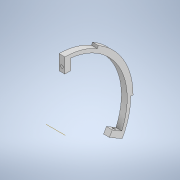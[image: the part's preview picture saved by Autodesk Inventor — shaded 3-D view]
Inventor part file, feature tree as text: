
AUTODESK INVENTOR PART (.ipt)
format: ipt  version: 2021 (Build 250183000, 183)  size: 156,672 bytes
history: native  units: in
note: dims shown in document units (in); Inventor stores cm internally (conversion verified against a paired STEP export)
features: hole x2, other x2, sketch x2, extrude x1
ambient origin geometry x8: Origin, YZ Plane, XZ Plane, XY Plane, X Axis, Y Axis, Z Axis, Center Point
bodies: Body1 (feature_tree)
feature tree (7):
  extrude  "Extrusion2"  TaperAngle=30.0deg  [1 undecoded]
  hole  "Hole1"  [1 undecoded]
  hole  "Hole2"  [1 undecoded]
  other  "Insert Center"
  other  "Part"
  sketch  "Sketch5"  dims[d29=2.375in d32=30.0deg]
  sketch  "Sketch6"  dims[d34=2.175in d35=0.2in d37=60.0deg d38=2.175in d42=0.59in d44=0.4134in d45=2.2963in d46=0.2in d47=0.0in d48=0.3346in d49=0.096in d50=0.75in d51=0.172in d52=0.25in d53=0.5635in d54=0.484in d55=0.8108in d56=0.3346in d57=0.096in d58=0.75in d59=0.172in d60=0.25in d61=0.5635in d62=0.484in d63=0.8108in d64=0.0315in d33=0.0344in]
note: 3 required parameter values undecoded (feature->parameter linkage not recoverable at this tier; creation-order binding heuristic only, values carry confidence <= 0.55)
